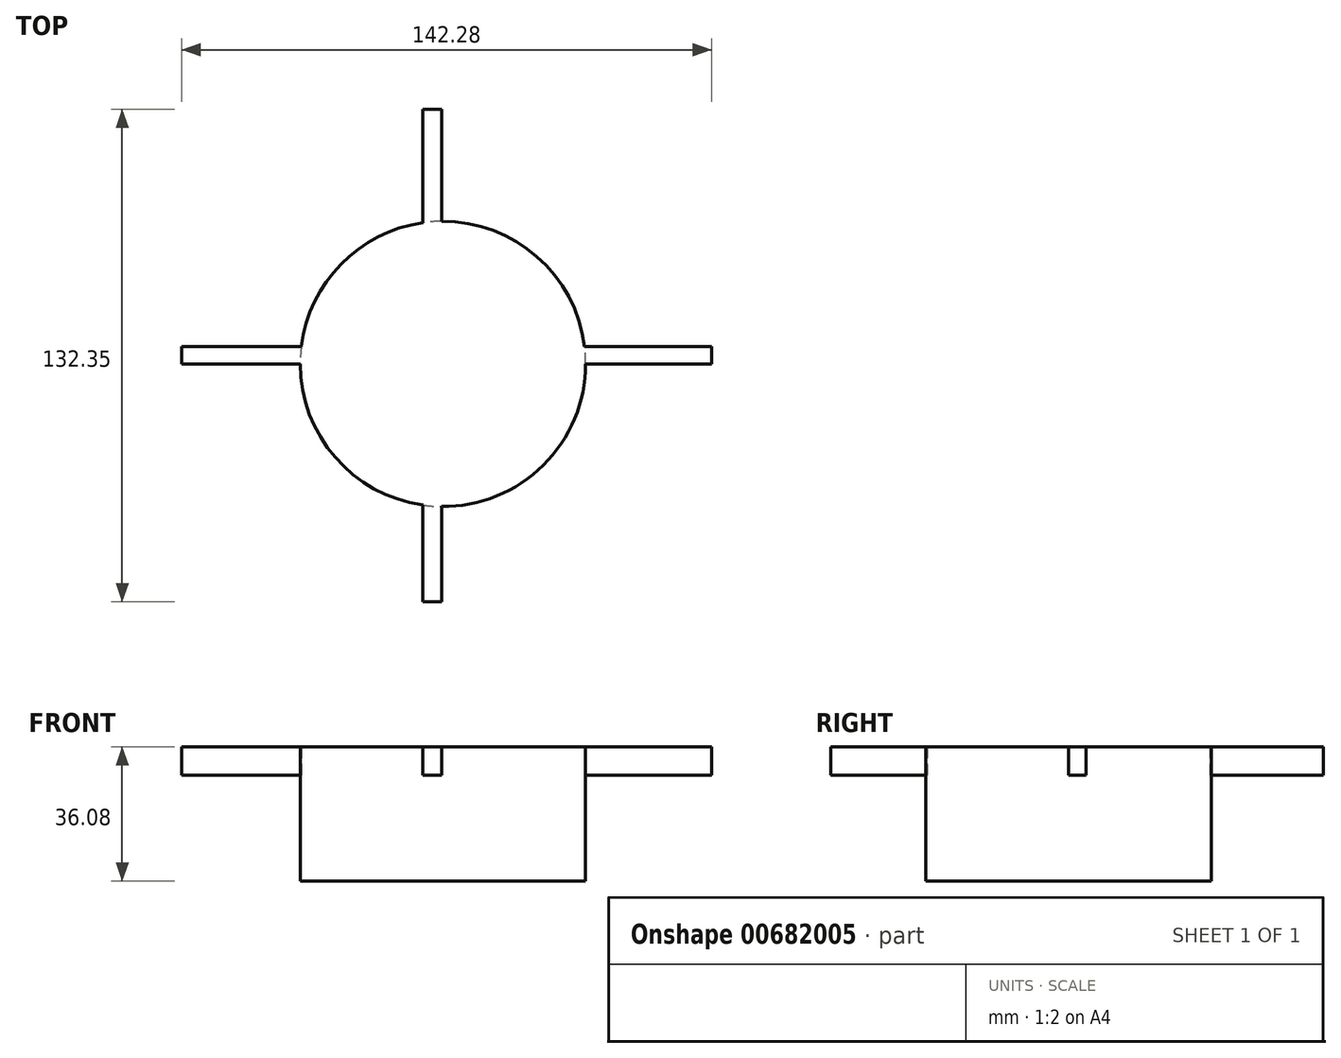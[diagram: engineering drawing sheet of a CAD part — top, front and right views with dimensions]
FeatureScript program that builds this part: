
annotation { "Feature Type Name" : "Feature", "Feature Type Description" : "" }
export const myFeature = defineFeature(function(context is Context, id is Id, definition is map)
    precondition{}
    {
        {
            var Q0;
            Q0=qCreatedBy(makeId("Front.planeOp"),FACE);
            var sketch = newSketch(context, id + "F0", { "sketchPlane" : qUnion([Q0])});
            skLineSegment(sketch, "E0.bottom", {"start": v(-27.75, 29.86) * mm, "end": v(10.57, 29.86) * mm});
            skLineSegment(sketch, "E0.top", {"start": v(-27.75, 25.53) * mm, "end": v(10.57, 25.53) * mm});
            skLineSegment(sketch, "E0.right", {"start": v(10.57, 29.86) * mm, "end": v(10.57, 25.53) * mm});
            skLineSegment(sketch, "E1.bottom", {"start": v(6.6, 25.53) * mm, "end": v(10.57, 25.53) * mm});
            skLineSegment(sketch, "E1.top", {"start": v(6.6, -78.4) * mm, "end": v(10.57, -78.4) * mm});
            skLineSegment(sketch, "E1.left", {"start": v(6.6, 25.53) * mm, "end": v(6.6, -78.4) * mm});
            skLineSegment(sketch, "E1.right", {"start": v(10.57, 25.53) * mm, "end": v(10.57, -78.4) * mm});
            skLineSegment(sketch, "E2", {"start": v(-27.75, 4.16) * mm, "end": v(-27.75, 41.15) * mm});
            skSolve(sketch);
        }
        {
            var Q0;
            {var subQ1=sQuery(id+"F0.wireOp",EDGE,"E0.bottom");Q0=makeQuery(id+"F0.imprint","IMPRINT",FACE,{"disambiguationData":[TD([[makeQuery(id+"F0.imprint","IMPRINT",EDGE,{"derivedFrom":subQ1}),-1.0]])]});}
            var Q1;
            Q1=makeQuery(id+"F0.imprint","IMPRINT",FACE,{"disambiguationData":[TD([[makeQuery(id+"F0.imprint","IMPRINT",EDGE,{"derivedFrom":sQuery(id+"F0.wireOp",EDGE,"E1.bottom")}),-1.0]])]});
            var Q2;
            Q2=sQuery(id+"F0.wireOp",EDGE,"E2");
            revolve(context, id + "F1", {"entities" : qUnion([Q0, Q1]), "axis" : qUnion([Q2]), "revolveType" : RevolveType.FULL});
        }
        {
            var Q0;
            Q0=makeQuery(id+"F1.opRevolve","SWEPT_FACE",FACE,{"disambiguationData":[OSD([sQuery(id+"F0.wireOp",EDGE,"E0.bottom")])]});
            extrude(context, id + "F2", {"entities" : qUnion([Q0]), "operationType" : NewBodyOperationType.ADD, "depth" : 31.75 * mm, "offsetDistance" : 25.4 * mm});
        }
        {
            var Q0;
            Q0=makeQuery(id+"F2.opExtrude","CAP_FACE",FACE,{"disambiguationData":[OSD([sQuery(id+"F0.wireOp",EDGE,"E0.bottom")])],"isStart":false});
            var sketch = newSketch(context, id + "F3", { "sketchPlane" : qUnion([Q0])});
            skLineSegment(sketch, "E3.bottom", {"start": v(-97.9, 4.66) * mm, "end": v(44.37, 4.66) * mm});
            skLineSegment(sketch, "E3.top", {"start": v(-97.9, 0) * mm, "end": v(44.37, 0) * mm});
            skLineSegment(sketch, "E3.left", {"start": v(-97.9, 4.66) * mm, "end": v(-97.9, 0) * mm});
            skLineSegment(sketch, "E3.right", {"start": v(44.37, 4.66) * mm, "end": v(44.37, 0) * mm});
            skLineSegment(sketch, "E4.bottom", {"start": v(-33.24, 68.43) * mm, "end": v(-28.15, 68.43) * mm});
            skLineSegment(sketch, "E4.top", {"start": v(-33.24, -63.92) * mm, "end": v(-28.15, -63.92) * mm});
            skLineSegment(sketch, "E4.left", {"start": v(-33.24, 68.43) * mm, "end": v(-33.24, -63.92) * mm});
            skLineSegment(sketch, "E4.right", {"start": v(-28.15, 68.43) * mm, "end": v(-28.15, -63.92) * mm});
            skSolve(sketch);
        }
        {
            var Q0;
            Q0 = qSketchRegion(id + "F3", true);
            extrude(context, id + "F4", {"entities" : qUnion([Q0]), "operationType" : NewBodyOperationType.ADD, "oppositeDirection" : true, "depth" : 7.62 * mm, "offsetDistance" : 25.4 * mm});
        }
    });
